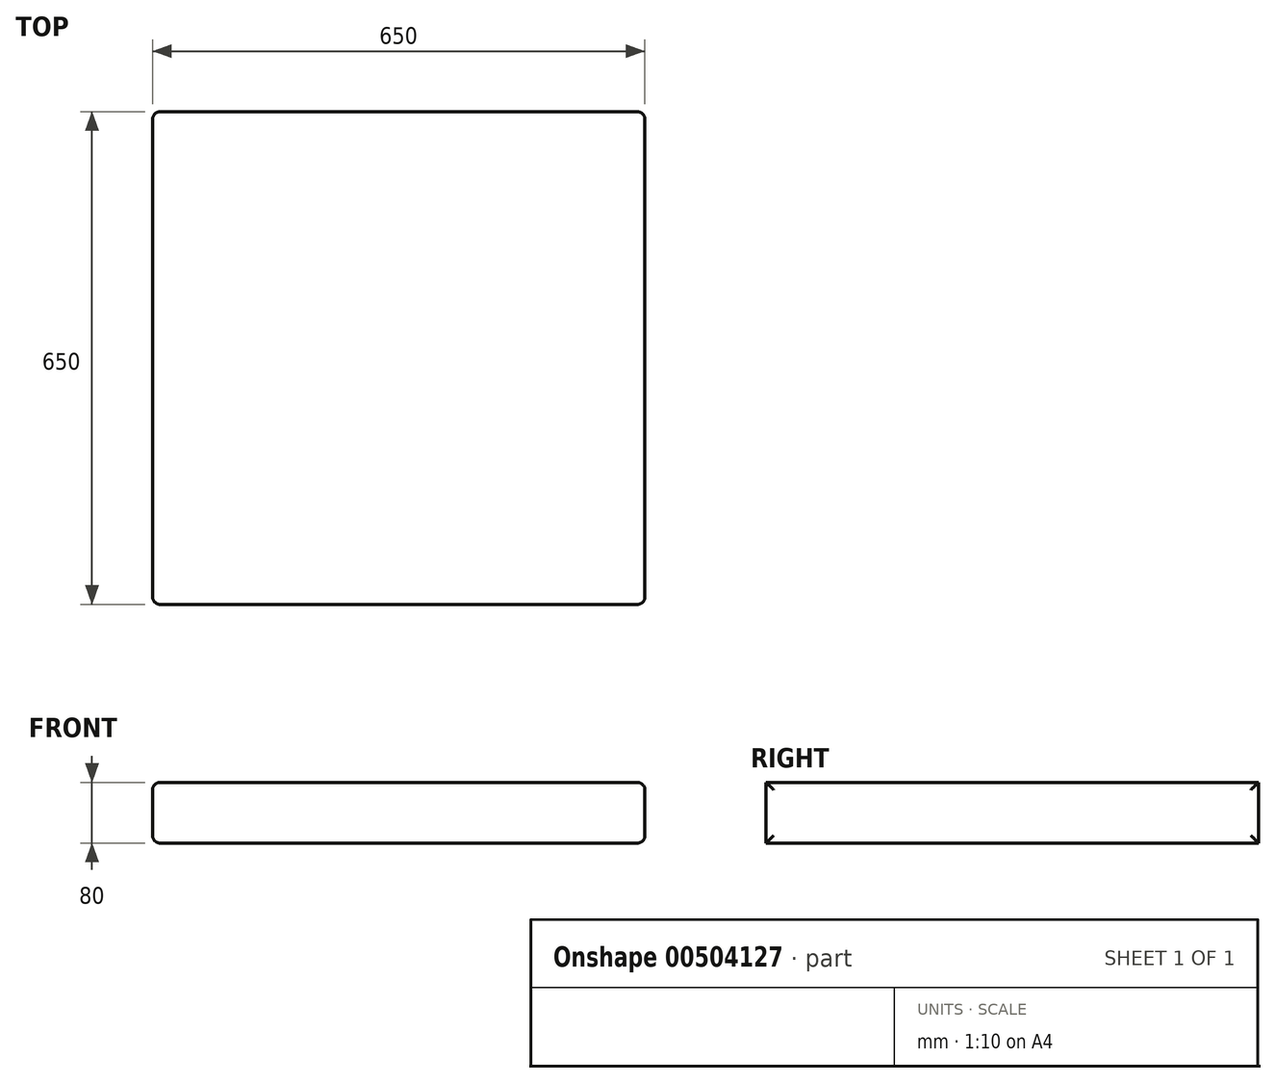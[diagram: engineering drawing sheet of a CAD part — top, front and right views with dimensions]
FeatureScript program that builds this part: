
annotation { "Feature Type Name" : "Feature", "Feature Type Description" : "" }
export const myFeature = defineFeature(function(context is Context, id is Id, definition is map)
    precondition{}
    {
        {
            var Q0;
            Q0=qCreatedBy(makeId("Top.planeOp"),FACE);
            var sketch = newSketch(context, id + "F0", { "sketchPlane" : qUnion([Q0])});
            skLineSegment(sketch, "E0.bottom", {"start": v(-325, 325) * mm, "end": v(325, 325) * mm});
            skLineSegment(sketch, "E0.top", {"start": v(-325, -325) * mm, "end": v(325, -325) * mm});
            skLineSegment(sketch, "E0.left", {"start": v(-325, 325) * mm, "end": v(-325, -325) * mm});
            skLineSegment(sketch, "E0.right", {"start": v(325, 325) * mm, "end": v(325, -325) * mm});
            skPoint(sketch, "E0.middle", {"position": v(0, 0) * mm});
            skSolve(sketch);
        }
        {
            var Q0;
            Q0 = qSketchRegion(id + "F0", true);
            extrude(context, id + "F1", {"entities" : qUnion([Q0]), "depth" : 80 * mm});
        }
        {
            var Q0;
            Q0=makeQuery(id+"F1.opExtrude","SWEPT_EDGE",EDGE,{"disambiguationData":[OSD([sQuery(id+"F0.wireOp",EDGE,"E0.top"),sQuery(id+"F0.wireOp",EDGE,"E0.left")])]});
            var Q1;
            Q1=makeQuery(id+"F1.opExtrude","SWEPT_EDGE",EDGE,{"disambiguationData":[OSD([sQuery(id+"F0.wireOp",EDGE,"E0.top"),sQuery(id+"F0.wireOp",EDGE,"E0.right")])]});
            var Q2;
            Q2=makeQuery(id+"F1.opExtrude","SWEPT_EDGE",EDGE,{"disambiguationData":[OSD([sQuery(id+"F0.wireOp",EDGE,"E0.bottom"),sQuery(id+"F0.wireOp",EDGE,"E0.right")])]});
            var Q3;
            Q3=makeQuery(id+"F1.opExtrude","SWEPT_EDGE",EDGE,{"disambiguationData":[OSD([sQuery(id+"F0.wireOp",EDGE,"E0.bottom"),sQuery(id+"F0.wireOp",EDGE,"E0.left")])]});
            var Q4;
            Q4=makeQuery(id+"F1.opExtrude","CAP_EDGE",EDGE,{"disambiguationData":[OSD([sQuery(id+"F0.wireOp",EDGE,"E0.left")])],"isStart":false});
            var Q5;
            Q5=makeQuery(id+"F1.opExtrude","CAP_EDGE",EDGE,{"disambiguationData":[OSD([sQuery(id+"F0.wireOp",EDGE,"E0.right")])],"isStart":false});
            var Q6;
            Q6=makeQuery(id+"F1.opExtrude","CAP_EDGE",EDGE,{"disambiguationData":[OSD([sQuery(id+"F0.wireOp",EDGE,"E0.right")])],"isStart":true});
            var Q7;
            Q7=makeQuery(id+"F1.opExtrude","CAP_EDGE",EDGE,{"disambiguationData":[OSD([sQuery(id+"F0.wireOp",EDGE,"E0.left")])],"isStart":true});
            fillet(context, id + "F2", {"entities" : qUnion([Q0, Q1, Q2, Q3, Q4, Q5, Q6, Q7]), "radius" : 10 * mm, "tangentPropagation" : true, "allowEdgeOverflow" : false});
        }
    });
